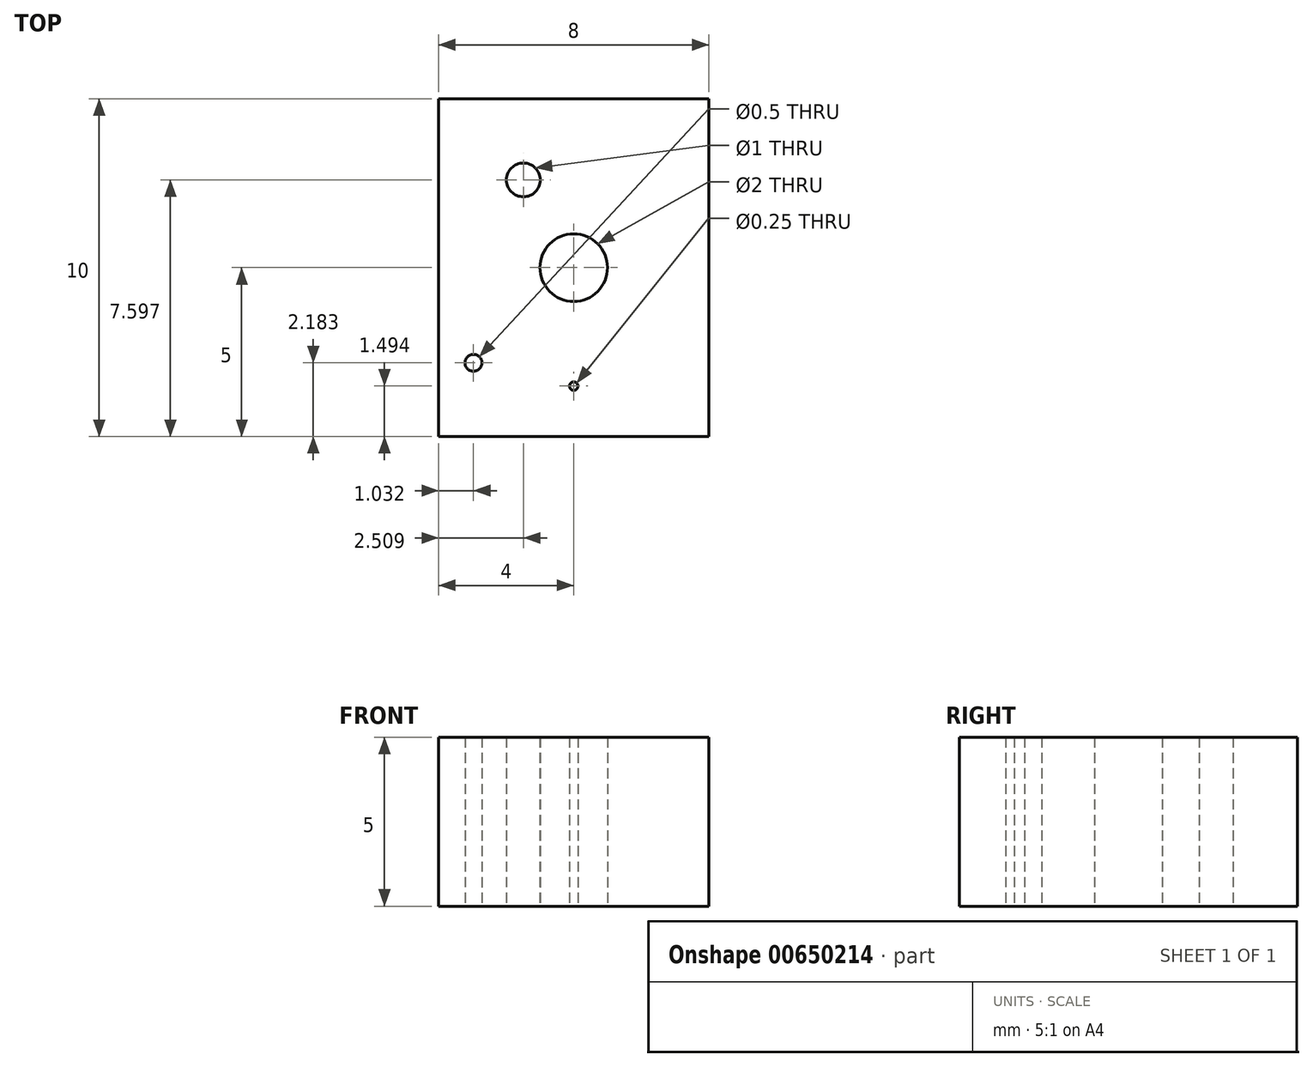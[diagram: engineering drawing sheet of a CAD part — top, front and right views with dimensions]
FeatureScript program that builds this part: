
annotation { "Feature Type Name" : "Feature", "Feature Type Description" : "" }
export const myFeature = defineFeature(function(context is Context, id is Id, definition is map)
    precondition{}
    {
        {
            var Q0;
            Q0=qCreatedBy(makeId("Top.planeOp"),FACE);
            var sketch = newSketch(context, id + "F0", { "sketchPlane" : qUnion([Q0])});
            skLineSegment(sketch, "E0.bottom", {"start": v(4, 5) * mm, "end": v(-4, 5) * mm});
            skLineSegment(sketch, "E0.top", {"start": v(4, -5) * mm, "end": v(-4, -5) * mm});
            skLineSegment(sketch, "E0.left", {"start": v(4, 5) * mm, "end": v(4, -5) * mm});
            skLineSegment(sketch, "E0.right", {"start": v(-4, 5) * mm, "end": v(-4, -5) * mm});
            skPoint(sketch, "E0.middle", {"position": v(0, 0) * mm});
            skCircle(sketch, "E1", {"center": v(0, 0) * mm, "radius": 1 * mm});
            skCircle(sketch, "E2", {"center": v(-1.5, 2.6) * mm, "radius": 0.5 * mm});
            skCircle(sketch, "E3", {"center": v(-2.97, -2.82) * mm, "radius": 0.25 * mm});
            skCircle(sketch, "E4", {"center": v(0, -3.5) * mm, "radius": 0.13 * mm});
            skSolve(sketch);
        }
        {
            var Q0;
            Q0=makeQuery(id+"F0.imprint","IMPRINT",FACE,{"disambiguationData":[TD([[makeQuery(id+"F0.imprint","IMPRINT",EDGE,{"derivedFrom":sQuery(id+"F0.wireOp",EDGE,"E0.bottom")}),1.0]])]});
            extrude(context, id + "F1", {"entities" : qUnion([Q0]), "depth" : 5 * mm, "offsetDistance" : 25 * mm});
        }
    });
